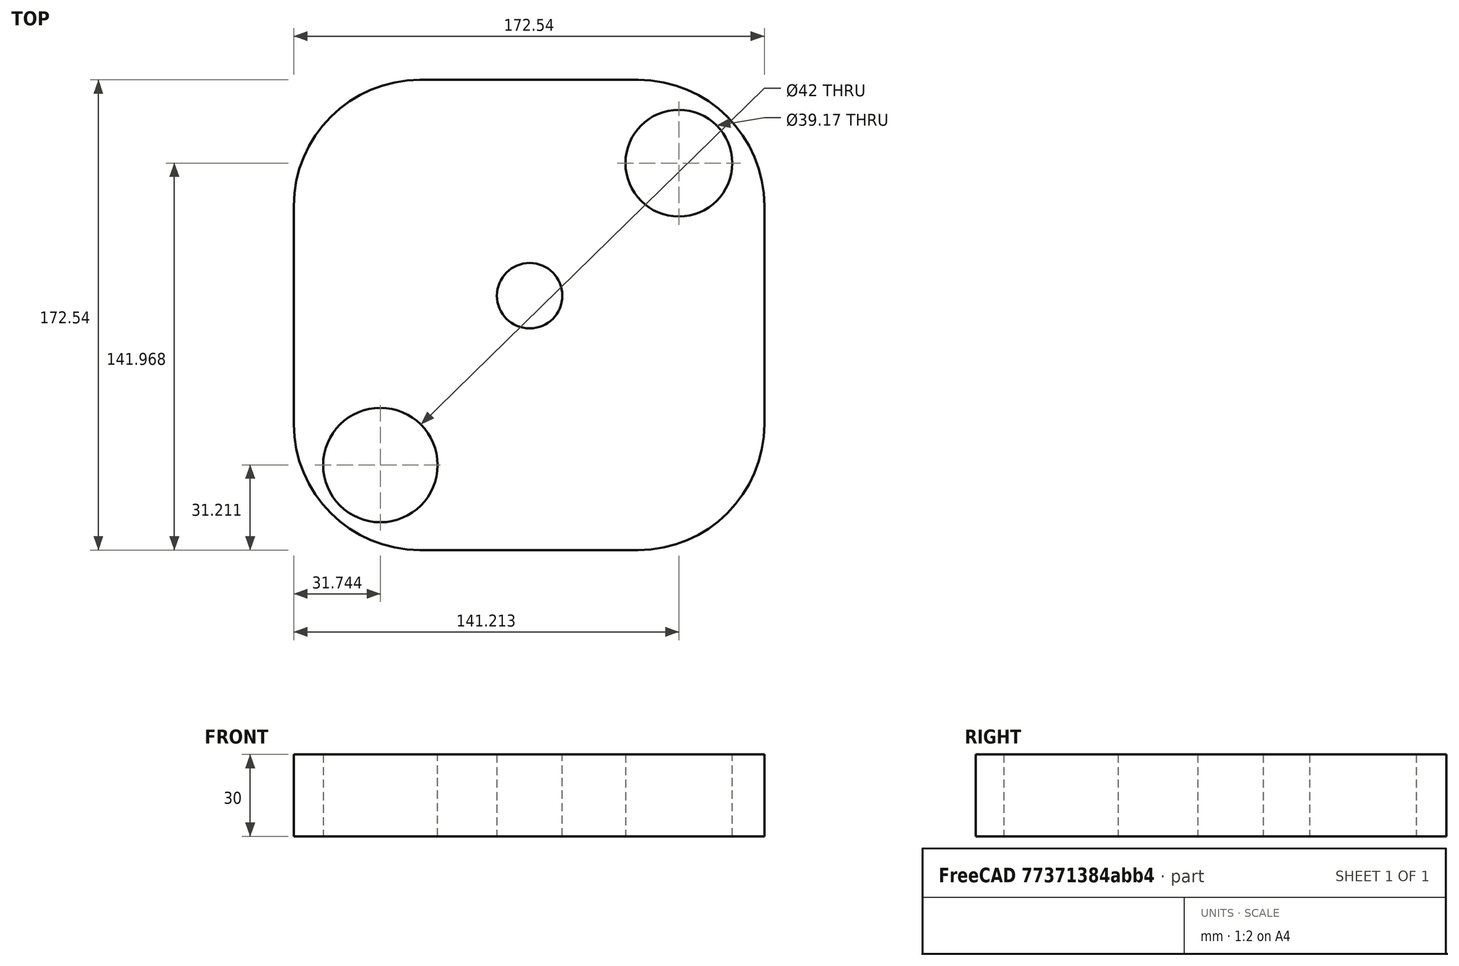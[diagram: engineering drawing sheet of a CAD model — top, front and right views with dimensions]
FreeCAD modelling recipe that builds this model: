
FCSTD DOCUMENT  (FreeCAD 0.18R16131 (Git))
Label: Momentum_Mold_Plate_160X200_12T(lm12uu)_Base
License: All rights reserved
LicenseURL: http://en.wikipedia.org/wiki/All_rights_reserved
objects: PartDesign::Pad×2, Sketcher::SketchObject×1, PartDesign::Body×1
note: 6 computed .brp shape members not serialized (recipe doc carries the construction recipe); baked Part::Feature solids carry a one-line shape summary decoded from their .brp

FEATURE [Sketcher::SketchObject] Sketch
  MapMode = 5
  Support = -> [XY_Plane]
  sketch-geometry (11):
    g0: LineSegment StartX=-35.5842 StartY=-63.1111 StartZ=0 EndX=44.4158 EndY=-63.1111 EndZ=0
    g1: LineSegment StartX=90.685 StartY=-16.8419 StartZ=0 EndX=90.685 EndY=63.1581 EndZ=0
    g2: LineSegment StartX=44.4158 StartY=109.427 StartZ=0 EndX=-35.5842 EndY=109.427 EndZ=0
    g3: LineSegment StartX=-81.8534 StartY=63.1581 StartZ=0 EndX=-81.8534 EndY=-16.8419 EndZ=0
    g4: Circle CenterX=4.62833 CenterY=30.2412 CenterZ=0 NormalX=0 NormalY=0 NormalZ=1 AngleXU=0 Radius=12
    g5: Circle CenterX=-50.1062 CenterY=-31.8986 CenterZ=0 NormalX=0 NormalY=0 NormalZ=1 AngleXU=0 Radius=21
    g6: Circle CenterX=59.3629 CenterY=78.8583 CenterZ=0 NormalX=0 NormalY=0 NormalZ=1 AngleXU=0 Radius=19.5845
    g7: ArcOfCircle CenterX=-35.5842 CenterY=63.1581 CenterZ=0 NormalX=0 NormalY=0 NormalZ=1 AngleXU=0 Radius=46.2692 StartAngle=1.5708 EndAngle=3.14159
    g8: ArcOfCircle CenterX=44.4158 CenterY=63.1581 CenterZ=0 NormalX=0 NormalY=0 NormalZ=1 AngleXU=0 Radius=46.2692 StartAngle=1e-16 EndAngle=1.5708
    g9: ArcOfCircle CenterX=44.4158 CenterY=-16.8419 CenterZ=0 NormalX=0 NormalY=0 NormalZ=1 AngleXU=0 Radius=46.2692 StartAngle=4.71239 EndAngle=6.28319
    g10: ArcOfCircle CenterX=-35.5842 CenterY=-16.8419 CenterZ=0 NormalX=0 NormalY=0 NormalZ=1 AngleXU=0 Radius=46.2692 StartAngle=3.14159 EndAngle=4.71239
  constraints (19):
    c: Horizontal(g0)
    c: Horizontal(g2)
    c: Vertical(g1)
    c: Vertical(g3)
    c: Radius(g4) = 12
    c: Radius(g5) = 21
    c: Tangent(g2,g7) = -1.5708
    c: Tangent(g3,g7) = -1.5708
    c: Tangent(g2,g8) = -1.5708
    c: Tangent(g1,g8) = -1.5708
    c: Tangent(g1,g9) = -1.5708
    c: Tangent(g0,g9) = -1.5708
    c: Tangent(g0,g10) = -1.5708
    c: Tangent(g3,g10) = -1.5708
    c: Vertical(g7,g10)
    c: DistanceY(g1,g1) = 80
    c: DistanceY(g3,g3) = 80
    c: Horizontal(g1,g3)
    c: DistanceX(g2,g2) = 80
FEATURE [PartDesign::Pad] Pad
  Length = 30
  Length2 = 100
  Profile = -> Sketch
  Type = 0
FEATURE [PartDesign::Pad] Pad001
  BaseFeature = -> Pad
  Length = 30
  Length2 = 100
  Profile = -> Sketch
  Type = 0
FEATURE [PartDesign::Body] Body
  Group = -> [Sketch,Pad,Pad001]
  Origin = -> Origin
  Tip = -> Pad001
